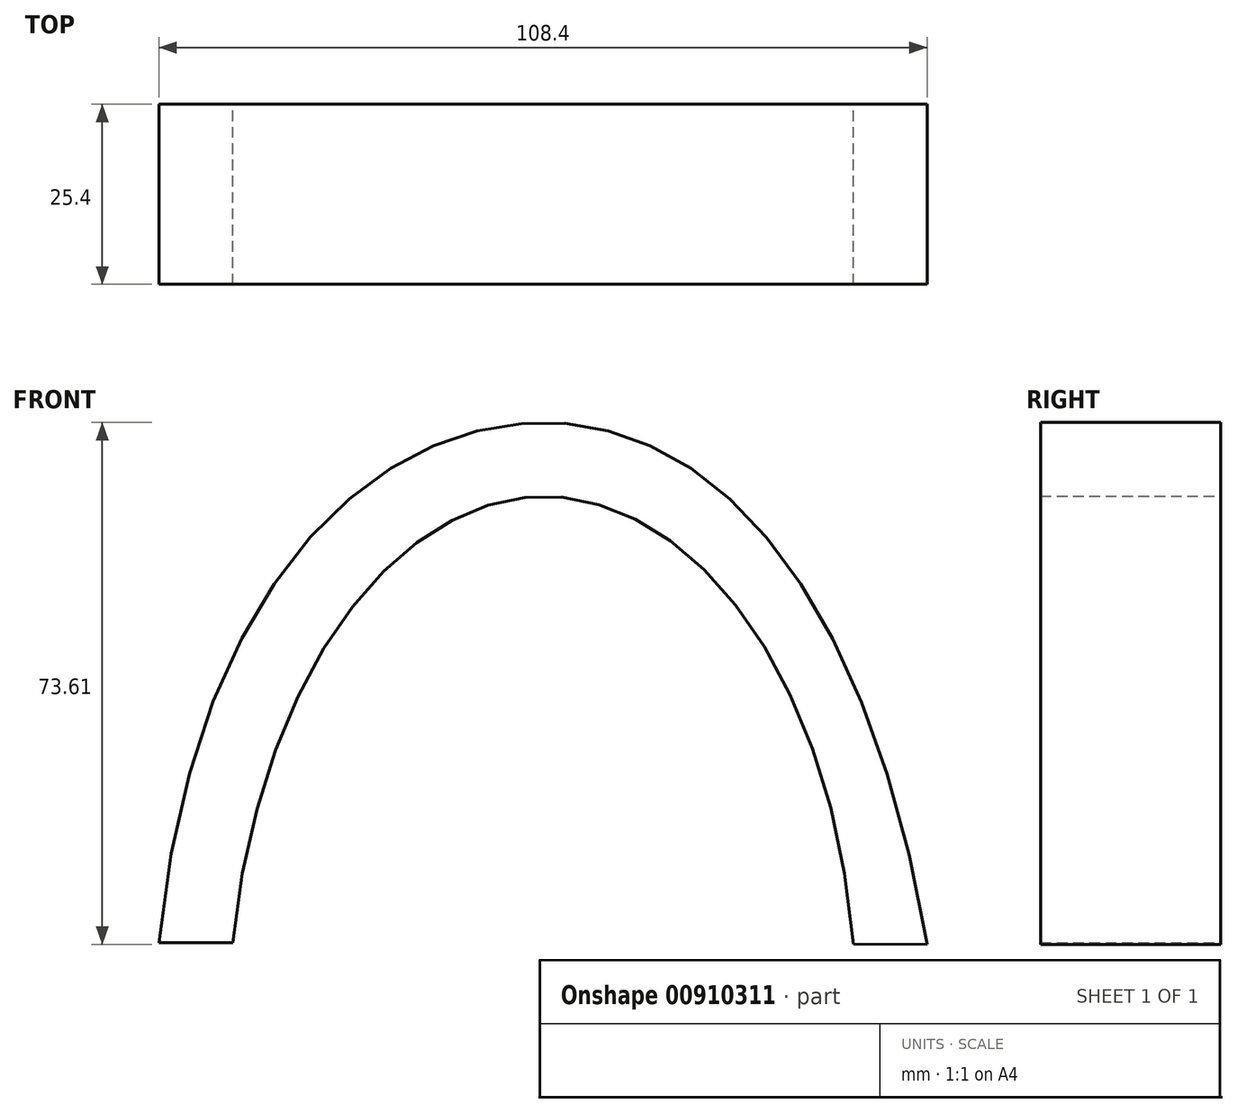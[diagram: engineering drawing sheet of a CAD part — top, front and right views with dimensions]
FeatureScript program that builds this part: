
annotation { "Feature Type Name" : "Feature", "Feature Type Description" : "" }
export const myFeature = defineFeature(function(context is Context, id is Id, definition is map)
    precondition{}
    {
        {
            var Q0;
            Q0=qCreatedBy(makeId("Front.planeOp"),FACE);
            var sketch = newSketch(context, id + "F0", { "sketchPlane" : qUnion([Q0])});
            skFitSpline(sketch, "E0", {"points": [v(-43.8, -31.2) * mm, v(0, 31.76) * mm, v(43.78, -31.36) * mm], "startDerivative": vector(23.83, 233.06) * mm, "endDerivative": vector(19.95, -237.07) * mm});
            skPoint(sketch, "E1.end.orphan", {"position": v(43.78, -30.75) * mm});
            skFitSpline(sketch, "E2", {"points": [v(-54.21, -31.2) * mm, v(0, 42.18) * mm, v(54.2, -31.43) * mm], "startDerivative": vector(29.37, 303.6) * mm, "endDerivative": vector(51.83, -305.14) * mm});
            skLineSegment(sketch, "E3", {"start": v(-54.21, -31.2) * mm, "end": v(-43.8, -31.2) * mm});
            skLineSegment(sketch, "E4", {"start": v(43.78, -31.36) * mm, "end": v(54.2, -31.43) * mm});
            skSolve(sketch);
        }
        {
            var Q0;
            Q0 = qSketchRegion(id + "F0", true);
            extrude(context, id + "F1", {"entities" : qUnion([Q0]), "depth" : 25.4 * mm, "offsetDistance" : 25.4 * mm});
        }
    });
